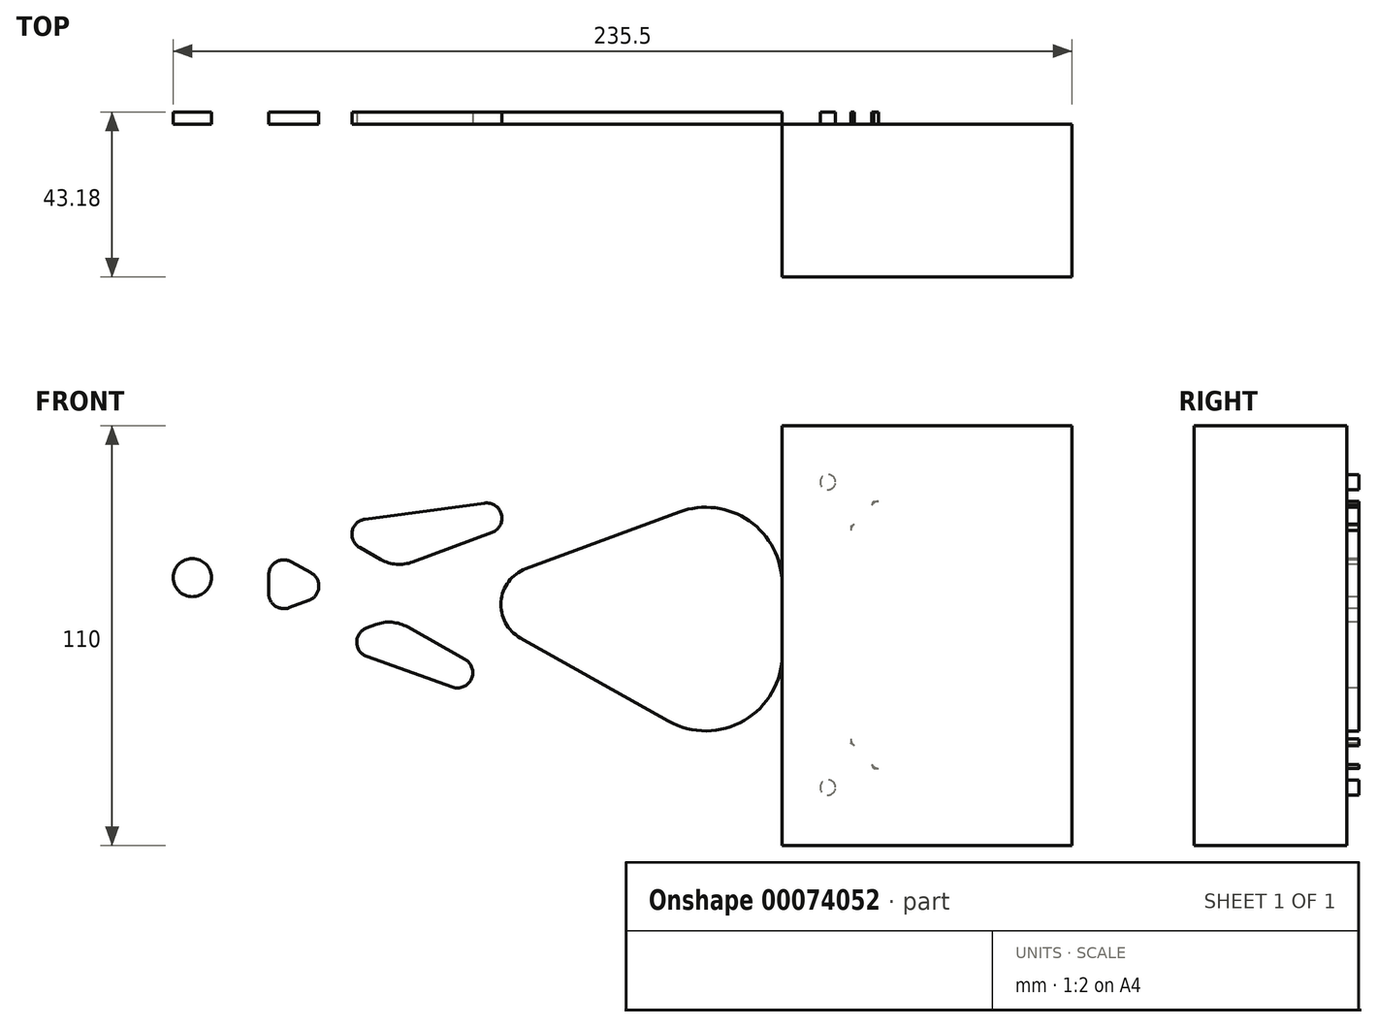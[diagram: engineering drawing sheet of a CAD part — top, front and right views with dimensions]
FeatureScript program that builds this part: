
annotation { "Feature Type Name" : "Feature", "Feature Type Description" : "" }
export const myFeature = defineFeature(function(context is Context, id is Id, definition is map)
    precondition{}
    {
        {
            var Q0;
            Q0=qCreatedBy(makeId("Front.planeOp"),FACE);
            var sketch = newSketch(context, id + "F0", { "sketchPlane" : qUnion([Q0])});
            skCircle(sketch, "E0", {"center": v(-192.5, 37) * mm, "radius": 5 * mm});
            skLineSegment(sketch, "E1", {"start": v(-192.5, 37) * mm, "end": v(0, 37) * mm, "construction": true});
            skLineSegment(sketch, "E2", {"start": v(0, -31) * mm, "end": v(0, 75) * mm, "construction": true});
            skLineSegment(sketch, "E3.rect.top", {"start": v(-38, -31) * mm, "end": v(-38, -31) * mm});
            skLineSegment(sketch, "E4", {"start": v(-192.5, 57) * mm, "end": v(-172.5, 57) * mm});
            skLineSegment(sketch, "E5", {"start": v(-172.5, 57) * mm, "end": v(-172.5, 57) * mm});
            skArc(sketch, "E6", {"start": v(-192.5, 57) * mm, "mid": v(-206.64, 22.86) * mm, "end": v(-172.5, 37) * mm, "construction": true});
            skArc(sketch, "E7", {"start": v(-172.5, 37) * mm, "mid": v(-178.36, 51.14) * mm, "end": v(-192.5, 57) * mm, "construction": true});
            skLineSegment(sketch, "E8", {"start": v(-172.5, 37) * mm, "end": v(-172.5, 37) * mm});
            skLineSegment(sketch, "E9", {"start": v(-172.5, 17) * mm, "end": v(-172.5, 17) * mm});
            skCircle(sketch, "E10", {"center": v(-26, 62) * mm, "radius": 2 * mm});
            skCircle(sketch, "E11.1.0.0", {"center": v(-26, -18) * mm, "radius": 2 * mm});
            skLineSegment(sketch, "E11.direction1", {"start": v(-26, 62) * mm, "end": v(-26, -18) * mm, "construction": true});
            skPoint(sketch, "E12", {"position": v(-26, 22) * mm});
            skLineSegment(sketch, "E13", {"start": v(-26, 62) * mm, "end": v(-26, 75) * mm, "construction": true});
            skLineSegment(sketch, "E14", {"start": v(-26, -18) * mm, "end": v(-26, -31) * mm, "construction": true});
            skLineSegment(sketch, "E15", {"start": v(-38, 75) * mm, "end": v(0, 75) * mm});
            skLineSegment(sketch, "E16", {"start": v(-38, -31) * mm, "end": v(0, -31) * mm});
            skArc(sketch, "E17", {"start": v(-192.5, 57) * mm, "mid": v(-212.5, 37) * mm, "end": v(-192.5, 17) * mm});
            skLineSegment(sketch, "E18", {"start": v(-38, 75) * mm, "end": v(-38, -31) * mm, "construction": true});
            skLineSegment(sketch, "E19", {"start": v(-172.5, 57) * mm, "end": v(-38, 75) * mm});
            skLineSegment(sketch, "E20", {"start": v(-172.5, 17) * mm, "end": v(-38, -31) * mm});
            skLineSegment(sketch, "E21.1", {"start": v(-172.5, 37.66) * mm, "end": v(-172.5, 32.85) * mm});
            skLineSegment(sketch, "E22.0", {"start": v(-38, 35.41) * mm, "end": v(-38, 16.82) * mm});
            skPoint(sketch, "E23.visualSharp", {"position": v(-38, 69.64) * mm});
            skArc(sketch, "E23.filletArc", {"start": v(-38, 35.41) * mm, "mid": v(-46.58, 51.83) * mm, "end": v(-64.95, 54.17) * mm});
            skPoint(sketch, "E24.visualSharp", {"position": v(-38, -19.57) * mm});
            skArc(sketch, "E24.filletArc", {"start": v(-67.8, -0.61) * mm, "mid": v(-47.9, -0.44) * mm, "end": v(-38, 16.82) * mm});
            skPoint(sketch, "E25.visualSharp", {"position": v(-119.61, 31.95) * mm});
            skArc(sketch, "E25.filletArc", {"start": v(-105.13, 39.27) * mm, "mid": v(-111.63, 30.68) * mm, "end": v(-106.56, 21.18) * mm});
            skPoint(sketch, "E26.visualSharp", {"position": v(-150.38, 34.16) * mm});
            skArc(sketch, "E26.filletArc", {"start": v(-161.96, 31.01) * mm, "mid": v(-159.36, 34.45) * mm, "end": v(-161.4, 38.25) * mm});
            skPoint(sketch, "E27.visualSharp", {"position": v(-134.97, 40.8) * mm});
            skArc(sketch, "E27.filletArc", {"start": v(-143.14, 41.75) * mm, "mid": v(-139.02, 40.5) * mm, "end": v(-134.76, 41.1) * mm});
            skPoint(sketch, "E28.visualSharp", {"position": v(-136.33, 24.97) * mm});
            skArc(sketch, "E28.filletArc", {"start": v(-136.1, 24.03) * mm, "mid": v(-140.22, 25.28) * mm, "end": v(-144.48, 24.7) * mm});
            skPoint(sketch, "E29.visualSharp", {"position": v(-153.4, 17.61) * mm});
            skArc(sketch, "E29.filletArc", {"start": v(-146.81, 23.83) * mm, "mid": v(-149.42, 20.05) * mm, "end": v(-146.77, 16.3) * mm});
            skPoint(sketch, "E30.visualSharp", {"position": v(-152.92, 52.56) * mm});
            skArc(sketch, "E30.filletArc", {"start": v(-147.24, 52.3) * mm, "mid": v(-150.63, 49.1) * mm, "end": v(-148.67, 44.86) * mm});
            skPoint(sketch, "E31.visualSharp", {"position": v(-87.38, 61.33) * mm});
            skArc(sketch, "E31.filletArc", {"start": v(-114, 48.79) * mm, "mid": v(-111.5, 53.5) * mm, "end": v(-115.92, 56.5) * mm});
            skPoint(sketch, "E32.visualSharp", {"position": v(-91.12, -4.61) * mm});
            skArc(sketch, "E32.filletArc", {"start": v(-124.37, 8.32) * mm, "mid": v(-119.39, 10.43) * mm, "end": v(-121.06, 15.57) * mm});
            skPoint(sketch, "E33.visualSharp", {"position": v(-170.13, 25.64) * mm});
            skArc(sketch, "E33.filletArc", {"start": v(-172.5, 32.85) * mm, "mid": v(-170.78, 29.57) * mm, "end": v(-167.1, 29.1) * mm});
            skPoint(sketch, "E34.visualSharp", {"position": v(-171.02, 47.67) * mm});
            skArc(sketch, "E34.filletArc", {"start": v(-166.54, 41.14) * mm, "mid": v(-170.52, 41.1) * mm, "end": v(-172.5, 37.66) * mm});
            skLineSegment(sketch, "E35", {"start": v(-26, -18) * mm, "end": v(0, -18) * mm, "construction": true});
            skPoint(sketch, "E36.visualSharp", {"position": v(-20, 56) * mm});
            skPoint(sketch, "E37.visualSharp", {"position": v(-20, -12) * mm});
            skLineSegment(sketch, "E38", {"start": v(-192.5, 17) * mm, "end": v(-172.5, 17) * mm});
            skLineSegment(sketch, "E39", {"start": v(-172.5, 57) * mm, "end": v(-172.5, 17) * mm, "construction": true});
            skLineSegment(sketch, "E40.0", {"start": v(-20, 57) * mm, "end": v(-14, 57) * mm, "construction": true});
            skLineSegment(sketch, "E40.1", {"start": v(-20, 57) * mm, "end": v(-20, 50.47) * mm, "construction": true});
            skLineSegment(sketch, "E40.2", {"start": v(-20, -13) * mm, "end": v(-14, -13) * mm, "construction": true});
            skArc(sketch, "E41", {"start": v(-14, 57) * mm, "mid": v(-35.57, 70.8) * mm, "end": v(-20, 50.47) * mm, "construction": true});
            skArc(sketch, "E42", {"start": v(-20, 50.47) * mm, "mid": v(-16.43, 53.2) * mm, "end": v(-14, 57) * mm});
            skLineSegment(sketch, "E43", {"start": v(-20, 50.47) * mm, "end": v(-20, -6.47) * mm});
            skLineSegment(sketch, "E44", {"start": v(-14, 57) * mm, "end": v(0, 57) * mm});
            skArc(sketch, "E45", {"start": v(-19.07, 51) * mm, "mid": v(-19.75, 50.28) * mm, "end": v(-20, 49.31) * mm});
            skArc(sketch, "E46", {"start": v(-12.73, 57) * mm, "mid": v(-13.77, 56.71) * mm, "end": v(-14.5, 55.93) * mm});
            skArc(sketch, "E47", {"start": v(-20, -6.47) * mm, "mid": v(-35.57, -26.8) * mm, "end": v(-14, -13) * mm, "construction": true});
            skArc(sketch, "E48", {"start": v(-14, -13) * mm, "mid": v(-16.43, -9.2) * mm, "end": v(-20, -6.47) * mm});
            skLineSegment(sketch, "E49", {"start": v(-20, -6.47) * mm, "end": v(-20, -13) * mm, "construction": true});
            skLineSegment(sketch, "E50", {"start": v(-14, -13) * mm, "end": v(0, -13) * mm});
            skArc(sketch, "E51", {"start": v(-20, -5.31) * mm, "mid": v(-19.75, -6.28) * mm, "end": v(-19.07, -7) * mm});
            skArc(sketch, "E52", {"start": v(-14.5, -11.93) * mm, "mid": v(-13.77, -12.71) * mm, "end": v(-12.73, -13) * mm});
            skLineSegment(sketch, "E53", {"start": v(-182.5, 57) * mm, "end": v(-139.62, 32.9) * mm, "construction": true});
            skLineSegment(sketch, "E54", {"start": v(-182.5, 17) * mm, "end": v(-139.62, 32.9) * mm, "construction": true});
            skArc(sketch, "E55.0", {"start": v(-18.92, -14.27) * mm, "mid": v(-16.35, -17) * mm, "end": v(-12.73, -18) * mm, "construction": true});
            skLineSegment(sketch, "E56", {"start": v(-139.62, 32.9) * mm, "end": v(-26, 75) * mm, "construction": true});
            skLineSegment(sketch, "E57", {"start": v(-139.62, 32.9) * mm, "end": v(-26, -31) * mm, "construction": true});
            skLineSegment(sketch, "E58.0", {"start": v(-105.13, 39.27) * mm, "end": v(-64.95, 54.17) * mm});
            skLineSegment(sketch, "E58.1", {"start": v(-106.56, 21.18) * mm, "end": v(-67.8, -0.61) * mm});
            skArc(sketch, "E59.0", {"start": v(-18.92, -14.27) * mm, "mid": v(-16.35, -17) * mm, "end": v(-12.73, -18) * mm});
            skLineSegment(sketch, "E60.0", {"start": v(-136.1, 24.03) * mm, "end": v(-121.06, 15.57) * mm});
            skLineSegment(sketch, "E60.1", {"start": v(-146.81, 23.83) * mm, "end": v(-144.48, 24.7) * mm});
            skLineSegment(sketch, "E61.0", {"start": v(-139.1, 39.48) * mm, "end": v(-134.76, 41.1) * mm, "construction": true});
            skLineSegment(sketch, "E61.1", {"start": v(-179.56, 62.23) * mm, "end": v(-148.67, 44.86) * mm, "construction": true});
            skLineSegment(sketch, "E62.0", {"start": v(-184.59, 22.63) * mm, "end": v(-167.1, 29.1) * mm, "construction": true});
            skLineSegment(sketch, "E62.1", {"start": v(-185.44, 51.77) * mm, "end": v(-166.54, 41.14) * mm, "construction": true});
            skLineSegment(sketch, "E63", {"start": v(-146.77, 16.3) * mm, "end": v(-124.37, 8.32) * mm});
            skLineSegment(sketch, "E64", {"start": v(-167.1, 29.1) * mm, "end": v(-161.96, 31.01) * mm});
            skLineSegment(sketch, "E65", {"start": v(-161.96, 31.01) * mm, "end": v(-153.86, 34.01) * mm, "construction": true});
            skLineSegment(sketch, "E66", {"start": v(-166.54, 41.14) * mm, "end": v(-161.4, 38.25) * mm});
            skLineSegment(sketch, "E67", {"start": v(-161.4, 38.25) * mm, "end": v(-153.86, 34.01) * mm, "construction": true});
            skLineSegment(sketch, "E68", {"start": v(-114, 48.79) * mm, "end": v(-28.12, 80.61) * mm, "construction": true});
            skLineSegment(sketch, "E69", {"start": v(-134.76, 41.1) * mm, "end": v(-114, 48.79) * mm});
            skLineSegment(sketch, "E70", {"start": v(-143.14, 41.75) * mm, "end": v(-139.1, 39.48) * mm, "construction": true});
            skLineSegment(sketch, "E71", {"start": v(-148.67, 44.86) * mm, "end": v(-143.14, 41.75) * mm});
            skLineSegment(sketch, "E72", {"start": v(-147.24, 52.3) * mm, "end": v(-115.92, 56.5) * mm});
            skSolve(sketch);
        }
        {
            var Q0;
            Q0=qSketchRegion(id+"F0",true);
            extrude(context, id + "F1", {"entities" : qUnion([Q0]), "oppositeDirection" : true, "depth" : 3.17 * mm});
        }
        {
            var Q0;
            Q0=qCreatedBy(makeId("Front.planeOp"),FACE);
            var sketch = newSketch(context, id + "F2", { "sketchPlane" : qUnion([Q0])});
            skLineSegment(sketch, "E73.rect.bottom", {"start": v(38, -33.22) * mm, "end": v(-38, -33.22) * mm});
            skLineSegment(sketch, "E73.rect.top", {"start": v(38, 76.78) * mm, "end": v(-38, 76.78) * mm});
            skLineSegment(sketch, "E73.rect.left", {"start": v(38, -33.22) * mm, "end": v(38, 76.78) * mm});
            skLineSegment(sketch, "E73.rect.right", {"start": v(-38, -33.22) * mm, "end": v(-38, 76.78) * mm});
            skPoint(sketch, "E73.rect.middle", {"position": v(0, 21.78) * mm});
            skSolve(sketch);
        }
        {
            var Q0;
            Q0=qSketchRegion(id+"F2",true);
            extrude(context, id + "F3", {"entities" : qUnion([Q0]), "depth" : 40 * mm});
        }
    });
